# Revit family: P1000H3_Beam
name_source: partatom
category: Structural Framing
units: mm (PartAtom-declared; Revit-internal decimal feet)

## family parameters
Always export as geometry = No
Always vertical = Yes
Cut with Voids When Loaded = No
Material for Model Behavior = Steel
OmniClass Number = 23.25.30.11.14.14
OmniClass Title = Beams
Section Shape = Not Defined
Shared = Yes
Show family pre-cut in plan views = Yes
Structural Framing Length Roundoff = 0 "

## types (5) — shared parameters
Assembly Code = B10
Description = P1000H3 - Beam - 1-5/8" x 1-5/8", 12 Gauge; Round Holes on all three sides
Disclaimer = https://www.unistrut.us
Height = 1.625 "
Manufacturer = Atkore Unistrut
Model = P1000H3
Salsify ID1 = US-P1000H3
URL = https://www.atkore.com

## per-type parameters (varying)
| type | Part Number | Power-Strut Part Number | Structural Material | UPC-10ft | UPC-20ft | Unit Weight |
| P1000H3 GR | P1000H3 ZD |  | Zinc Dichromate |  | "786364060279" | 1.91 lb/ft |
| P1000H3 HG | P1000H3 HG |  | Hot Dip Galvanized | "786364896328" | "786364013473" | 1.75 lb/ft |
| P1000H3 PG | P1000H3 PG | PS 200 H3 PGAL | Pre-Galvanized | "0786364906270" | "78636401348" | 1.91 lb/ft |
| P1000H3 PL | P1000H3 PL |  | Plain | "786364013459" | "786364013497" | 1.75 lb/ft |
| P1000H3 ZD | P1000H3 ZD |  | Zinc Dichromate |  | "786364060279" | 1.91 lb/ft |

## geometry (parser evidence)
native form markers: Sweep x13
no freeform markers — native parametric forms only
